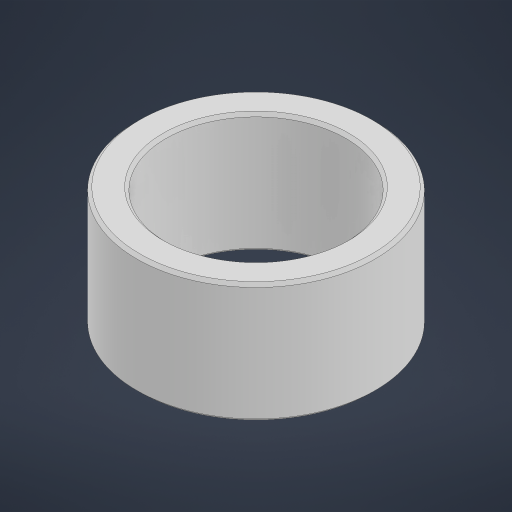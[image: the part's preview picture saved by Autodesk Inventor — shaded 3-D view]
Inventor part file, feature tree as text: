
AUTODESK INVENTOR PART (.ipt)
format: ipt  version: 2023 (Build 270158000, 158)  size: 178,176 bytes
history: native  units: in
note: dims shown in document units (in); Inventor stores cm internally (conversion verified against a paired STEP export)
features: chamfer x1
ambient origin geometry x8: Origin, YZ Plane, XZ Plane, XY Plane, X Axis, Y Axis, Z Axis, Center Point
bodies: Solid1 (feature_tree)
feature tree (1):
  chamfer  "Chamfer1"  [1 undecoded]
note: 1 required parameter value undecoded (feature->parameter linkage not recoverable at this tier; creation-order binding heuristic only, values carry confidence <= 0.55)
